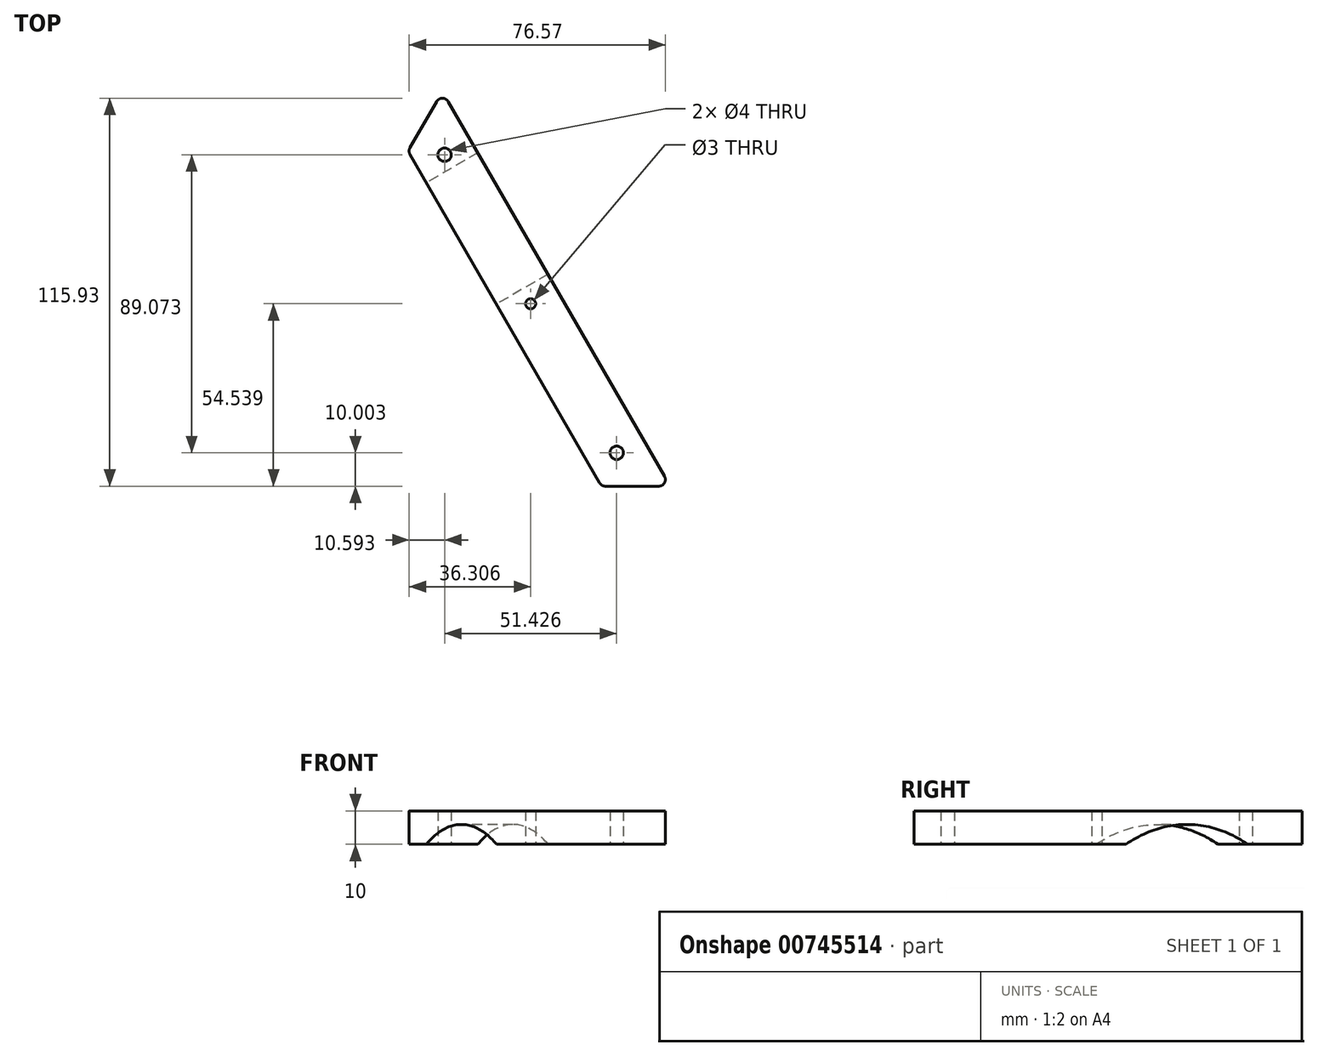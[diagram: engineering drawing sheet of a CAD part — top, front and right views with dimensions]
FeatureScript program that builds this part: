
annotation { "Feature Type Name" : "Feature", "Feature Type Description" : "" }
export const myFeature = defineFeature(function(context is Context, id is Id, definition is map)
    precondition{}
    {
        {
            var Q0;
            Q0=qCreatedBy(makeId("Top.planeOp"),FACE);
            var sketch = newSketch(context, id + "F0", { "sketchPlane" : qUnion([Q0])});
            skCircle(sketch, "E0", {"center": v(0, 0) * mm, "radius": 109.54 * mm, "construction": true});
            skLineSegment(sketch, "E1", {"start": v(-184.94, -106.78) * mm, "end": v(0, 213.55) * mm, "construction": true});
            skLineSegment(sketch, "E2", {"start": v(0, 213.55) * mm, "end": v(184.94, -106.78) * mm, "construction": true});
            skLineSegment(sketch, "E3", {"start": v(184.94, -106.78) * mm, "end": v(-184.94, -106.78) * mm, "construction": true});
            skLineSegment(sketch, "E4", {"start": v(0, 0) * mm, "end": v(-184.94, -106.78) * mm, "construction": true});
            skLineSegment(sketch, "E5", {"start": v(0, 0) * mm, "end": v(184.94, -106.78) * mm, "construction": true});
            skLineSegment(sketch, "E6", {"start": v(0, 213.55) * mm, "end": v(0, 0) * mm, "construction": true});
            skLineSegment(sketch, "E7.left", {"start": v(-48.73, -106.78) * mm, "end": v(-116.84, 11.19) * mm});
            skLineSegment(sketch, "E7.right", {"start": v(-69.26, -106.78) * mm, "end": v(-127.1, -6.6) * mm});
            skLineSegment(sketch, "E8", {"start": v(-127.1, -6.6) * mm, "end": v(-116.84, 11.19) * mm});
            skLineSegment(sketch, "E9", {"start": v(-48.73, -106.78) * mm, "end": v(-69.26, -106.78) * mm});
            skCircle(sketch, "E10", {"center": v(-90.48, -52.24) * mm, "radius": 1.5 * mm});
            skCircle(sketch, "E11", {"center": v(-64.77, -96.78) * mm, "radius": 2 * mm});
            skCircle(sketch, "E12", {"center": v(-116.2, -7.7) * mm, "radius": 2 * mm});
            skLineSegment(sketch, "E13", {"start": v(-59, -106.78) * mm, "end": v(-121.97, 2.3) * mm, "construction": true});
            skSolve(sketch);
        }
        {
            var Q0;
            Q0=qSketchRegion(id+"F0",true);
            extrude(context, id + "F1", {"entities" : qUnion([Q0]), "depth" : 10 * mm, "offsetDistance" : 25.4 * mm});
        }
        {
            var Q0;
            Q0=makeQuery(id+"FDzoLKtKOqV0GEJ_1.boolean.opBoolean","MERGE",EDGE,{"derivedFrom":[makeQuery(id+"F1.opExtrude","SWEPT_EDGE",EDGE,{"disambiguationData":[OSD([sQuery(id+"F0.wireOp",EDGE,"E7.right"),sQuery(id+"F0.wireOp",EDGE,"E8")])]}),makeQuery(id+"FDzoLKtKOqV0GEJ_1.opExtrude","SWEPT_EDGE",EDGE,{"disambiguationData":[OSD([sQuery(id+"FbQ5fZsY1d14WYz_1.wireOp",EDGE,"571813bc-1494-4deb-91fd-3bdaee0effb7.0.0"),sQuery(id+"FbQ5fZsY1d14WYz_1.wireOp",EDGE,"571813bc-1494-4deb-91fd-3bdaee0effb7.0.3")])]})]});
            var Q1;
            Q1=makeQuery(id+"FDzoLKtKOqV0GEJ_1.boolean.opBoolean","MERGE",EDGE,{"derivedFrom":[makeQuery(id+"F1.opExtrude","SWEPT_EDGE",EDGE,{"disambiguationData":[OSD([sQuery(id+"F0.wireOp",EDGE,"E7.right"),sQuery(id+"F0.wireOp",EDGE,"E9")])]}),makeQuery(id+"FDzoLKtKOqV0GEJ_1.opExtrude","SWEPT_EDGE",EDGE,{"disambiguationData":[OSD([sQuery(id+"FbQ5fZsY1d14WYz_1.wireOp",EDGE,"571813bc-1494-4deb-91fd-3bdaee0effb7.0.0"),sQuery(id+"FbQ5fZsY1d14WYz_1.wireOp",EDGE,"571813bc-1494-4deb-91fd-3bdaee0effb7.0.1")])]})]});
            var Q2;
            Q2=makeQuery(id+"FDzoLKtKOqV0GEJ_1.boolean.opBoolean","MERGE",EDGE,{"derivedFrom":[makeQuery(id+"F1.opExtrude","SWEPT_EDGE",EDGE,{"disambiguationData":[OSD([sQuery(id+"F0.wireOp",EDGE,"E7.left"),sQuery(id+"F0.wireOp",EDGE,"E9")])]}),makeQuery(id+"FDzoLKtKOqV0GEJ_1.opExtrude","SWEPT_EDGE",EDGE,{"disambiguationData":[OSD([sQuery(id+"FbQ5fZsY1d14WYz_1.wireOp",EDGE,"571813bc-1494-4deb-91fd-3bdaee0effb7.0.1"),sQuery(id+"FbQ5fZsY1d14WYz_1.wireOp",EDGE,"571813bc-1494-4deb-91fd-3bdaee0effb7.0.2")])]})]});
            var Q3;
            Q3=makeQuery(id+"FDzoLKtKOqV0GEJ_1.boolean.opBoolean","MERGE",EDGE,{"derivedFrom":[makeQuery(id+"F1.opExtrude","SWEPT_EDGE",EDGE,{"disambiguationData":[OSD([sQuery(id+"F0.wireOp",EDGE,"E7.left"),sQuery(id+"F0.wireOp",EDGE,"E8")])]}),makeQuery(id+"FDzoLKtKOqV0GEJ_1.opExtrude","SWEPT_EDGE",EDGE,{"disambiguationData":[OSD([sQuery(id+"FbQ5fZsY1d14WYz_1.wireOp",EDGE,"571813bc-1494-4deb-91fd-3bdaee0effb7.0.2"),sQuery(id+"FbQ5fZsY1d14WYz_1.wireOp",EDGE,"571813bc-1494-4deb-91fd-3bdaee0effb7.0.3")])]})]});
            fillet(context, id + "F2", {"entities" : qUnion([Q0, Q1, Q2, Q3]), "radius" : 2.03 * mm, "tangentPropagation" : true, "allowEdgeOverflow" : false});
        }
        {
            var Q0;
            Q0=makeQuery(id+"FDzoLKtKOqV0GEJ_1.boolean.opBoolean","MERGE",FACE,{"derivedFrom":[makeQuery(id+"F1.opExtrude","SWEPT_FACE",FACE,{"disambiguationData":[OSD([sQuery(id+"F0.wireOp",EDGE,"E7.right")])]}),makeQuery(id+"FDzoLKtKOqV0GEJ_1.opExtrude","SWEPT_FACE",FACE,{"disambiguationData":[OSD([sQuery(id+"FbQ5fZsY1d14WYz_1.wireOp",EDGE,"571813bc-1494-4deb-91fd-3bdaee0effb7.0.0")])]})]});
            var sketch = newSketch(context, id + "F3", { "sketchPlane" : qUnion([Q0])});
            skLineSegment(sketch, "E14", {"start": v(-1.5, 5) * mm, "end": v(-1.5, 10) * mm});
            skLineSegment(sketch, "E15", {"start": v(1.5, 10) * mm, "end": v(1.5, 5) * mm});
            skLineSegment(sketch, "E16", {"start": v(-53.43, 0) * mm, "end": v(-53.43, 10) * mm});
            skLineSegment(sketch, "E17", {"start": v(-49.43, 10) * mm, "end": v(-49.43, 0) * mm});
            skLineSegment(sketch, "E18", {"start": v(49.43, 0) * mm, "end": v(49.43, 10) * mm});
            skLineSegment(sketch, "E19", {"start": v(53.43, 10) * mm, "end": v(53.43, 0) * mm});
            skLineSegment(sketch, "E20", {"start": v(0, 0) * mm, "end": v(0, -36.75) * mm, "construction": true});
            skArc(sketch, "E21", {"start": v(-5, 0) * mm, "mid": v(-25.96, 5.93) * mm, "end": v(-46.93, 0) * mm});
            skSolve(sketch);
        }
        {
            var Q0;
            {var subQ0=sQuery(id+"F3.wireOp",EDGE,"E21");Q0=makeQuery(id+"F3.imprint","IMPRINT",FACE,{"disambiguationData":[TD([[makeQuery(id+"F3.imprint","IMPRINT",EDGE,{"derivedFrom":subQ0}),1.0]])]});}
            extrude(context, id + "F4", {"entities" : qUnion([Q0]), "operationType" : NewBodyOperationType.REMOVE, "endBound" : BoundingType.THROUGH_ALL, "oppositeDirection" : true, "depth" : 25.4 * mm, "offsetDistance" : 25.4 * mm});
        }
        {
            var Q0;
            Q0=makeQuery(id+"FDzoLKtKOqV0GEJ_1.boolean.opBoolean","MERGE",FACE,{"derivedFrom":[makeQuery(id+"F1.opExtrude","SWEPT_FACE",FACE,{"disambiguationData":[OSD([sQuery(id+"F0.wireOp",EDGE,"E8")])]}),makeQuery(id+"FDzoLKtKOqV0GEJ_1.opExtrude","SWEPT_FACE",FACE,{"disambiguationData":[OSD([sQuery(id+"FbQ5fZsY1d14WYz_1.wireOp",EDGE,"571813bc-1494-4deb-91fd-3bdaee0effb7.0.3")])]})]});
            var Q1;
            Q1=makeQuery(id+"FDzoLKtKOqV0GEJ_1.boolean.opBoolean","MERGE",FACE,{"derivedFrom":[makeQuery(id+"F1.opExtrude","SWEPT_FACE",FACE,{"disambiguationData":[OSD([sQuery(id+"F0.wireOp",EDGE,"E9")])]}),makeQuery(id+"FDzoLKtKOqV0GEJ_1.opExtrude","SWEPT_FACE",FACE,{"disambiguationData":[OSD([sQuery(id+"FbQ5fZsY1d14WYz_1.wireOp",EDGE,"571813bc-1494-4deb-91fd-3bdaee0effb7.0.1")])]})]});
            cPlane(context, id + "F5", {"entities" : qUnion([Q0, Q1]), "cplaneType" : CPlaneType.MID_PLANE, "offset" : 25.4 * mm, "width" : 152.4 * mm, "height" : 152.4 * mm});
        }
    });
